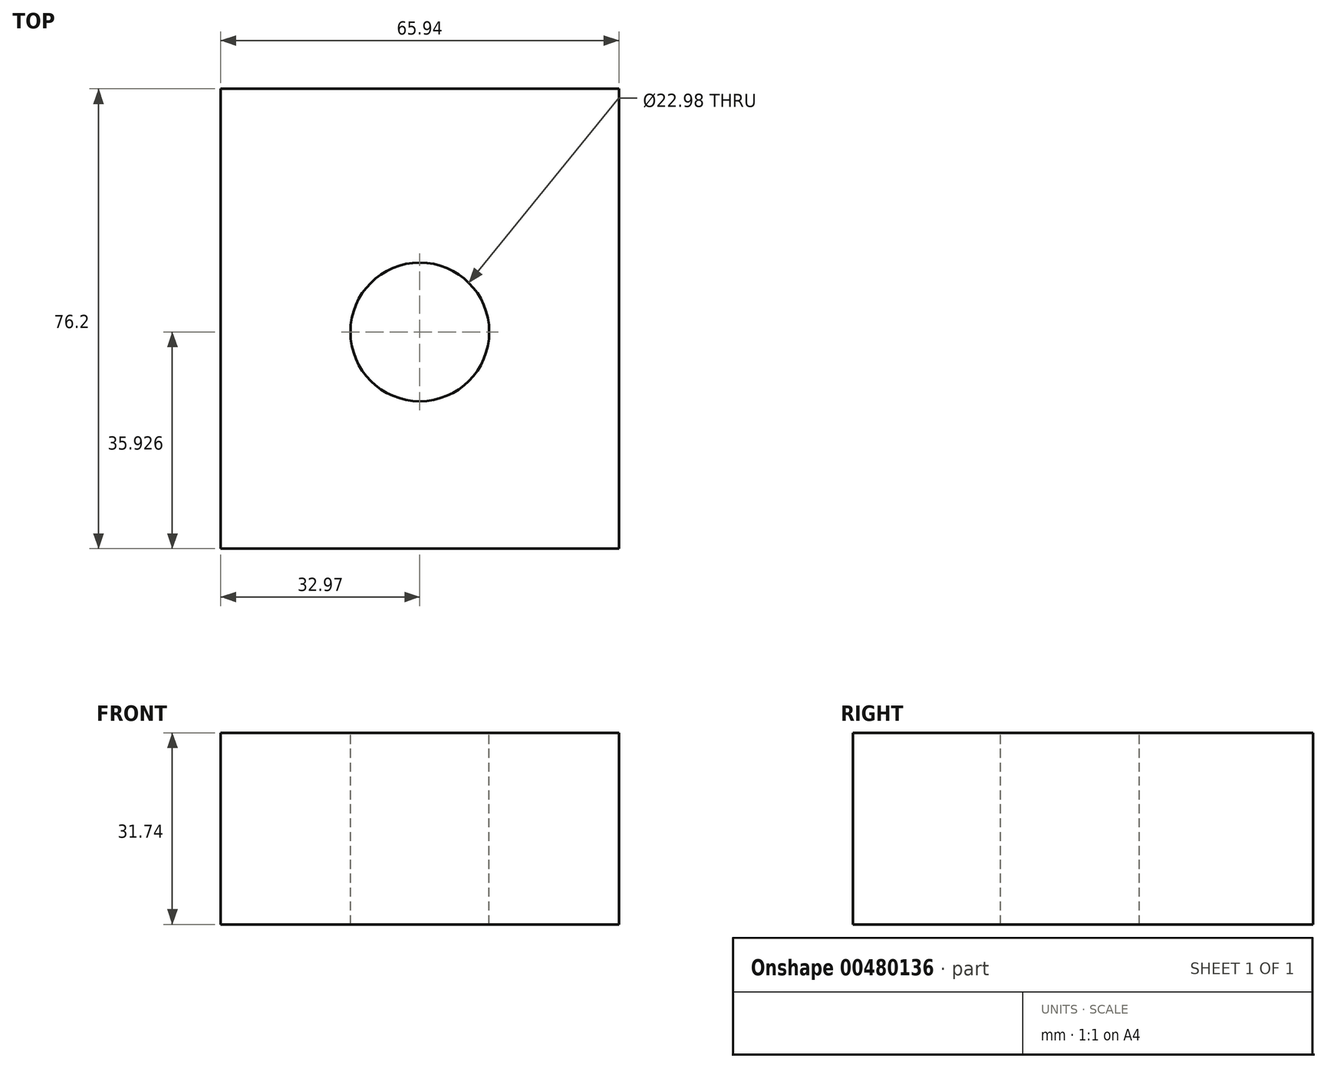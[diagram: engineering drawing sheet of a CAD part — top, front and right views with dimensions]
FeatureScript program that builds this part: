
annotation { "Feature Type Name" : "Feature", "Feature Type Description" : "" }
export const myFeature = defineFeature(function(context is Context, id is Id, definition is map)
    precondition{}
    {
        {
            var Q0;
            Q0=qCreatedBy(makeId("Front.planeOp"),FACE);
            var sketch = newSketch(context, id + "F0", { "sketchPlane" : qUnion([Q0])});
            skLineSegment(sketch, "E0.bottom", {"start": v(-32.97, 15.87) * mm, "end": v(32.97, 15.87) * mm});
            skLineSegment(sketch, "E0.top", {"start": v(-32.97, -15.87) * mm, "end": v(32.97, -15.87) * mm});
            skLineSegment(sketch, "E0.left", {"start": v(-32.97, 15.87) * mm, "end": v(-32.97, -15.87) * mm});
            skLineSegment(sketch, "E0.right", {"start": v(32.97, 15.87) * mm, "end": v(32.97, -15.87) * mm});
            skPoint(sketch, "E0.middle", {"position": v(0, 0) * mm});
            skSolve(sketch);
        }
        {
            var Q0;
            Q0 = qSketchRegion(id + "F0", true);
            extrude(context, id + "F1", {"entities" : qUnion([Q0]), "depth" : 76.2 * mm});
        }
        {
            var Q0;
            Q0=makeQuery(id+"F1.opExtrude","SWEPT_FACE",FACE,{"disambiguationData":[OSD([sQuery(id+"F0.wireOp",EDGE,"E0.bottom")])]});
            var sketch = newSketch(context, id + "F2", { "sketchPlane" : qUnion([Q0])});
            skCircle(sketch, "E1", {"center": v(0, -40.27) * mm, "radius": 11.5 * mm});
            skSolve(sketch);
        }
        {
            var Q0;
            Q0=makeQuery(id+"F2.imprint","IMPRINT",FACE,{"disambiguationData":[TD([[makeQuery(id+"F2.imprint","IMPRINT",EDGE,{"derivedFrom":sQuery(id+"F2.wireOp",EDGE,"E1")}),1.0]])]});
            extrude(context, id + "F3", {"entities" : qUnion([Q0]), "operationType" : NewBodyOperationType.REMOVE, "endBound" : BoundingType.THROUGH_ALL, "oppositeDirection" : true, "depth" : 25.4 * mm});
        }
    });
